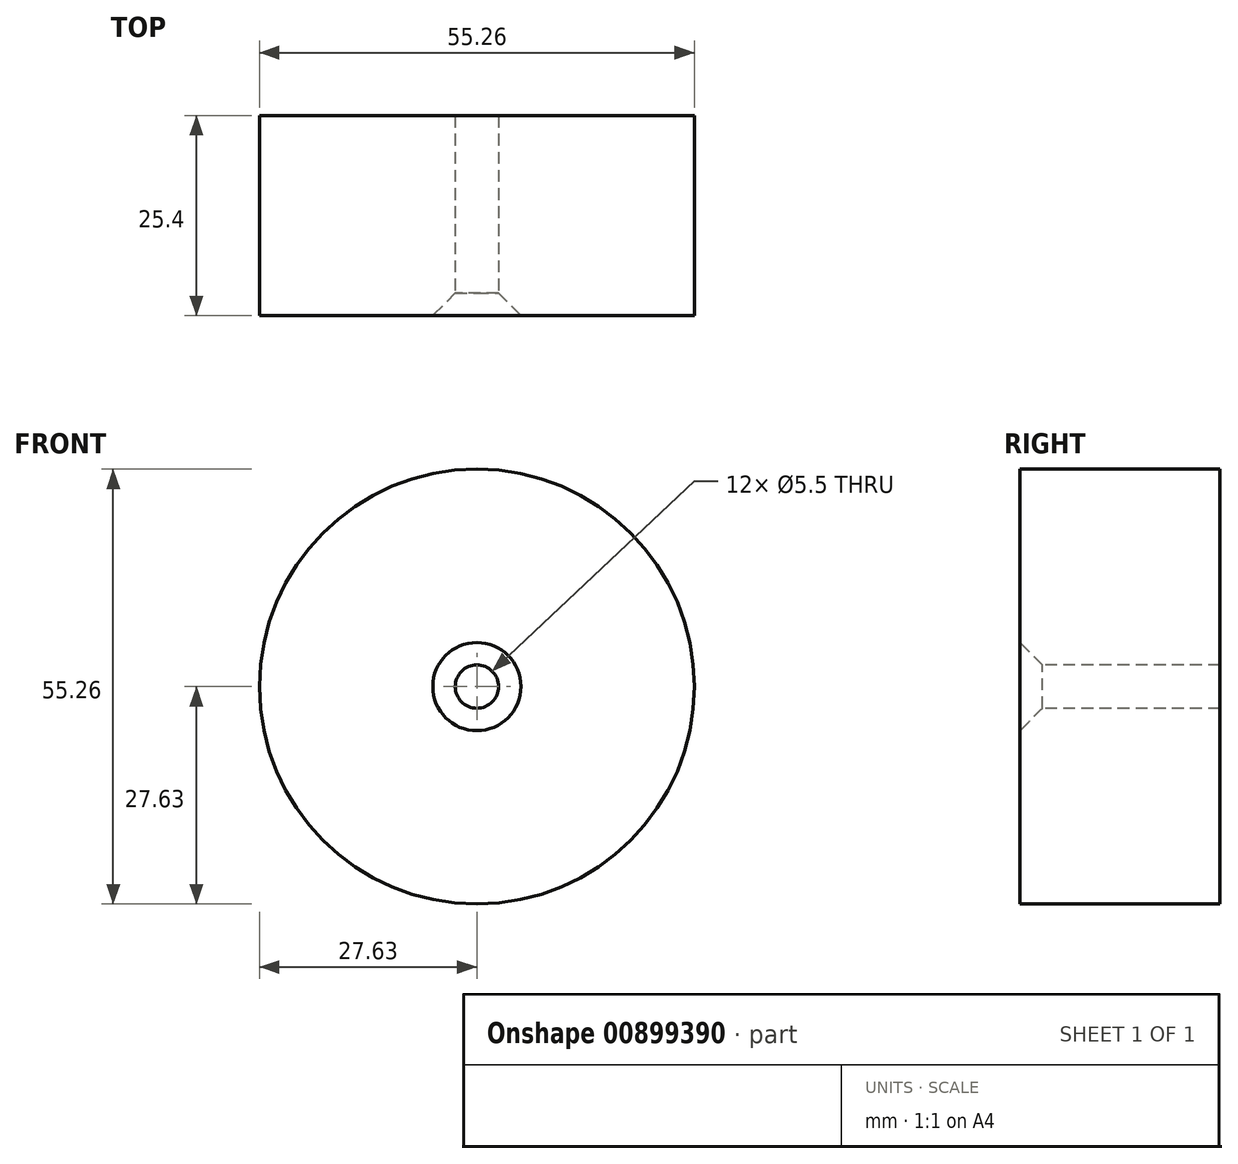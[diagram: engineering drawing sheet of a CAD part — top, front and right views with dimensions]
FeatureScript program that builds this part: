
annotation { "Feature Type Name" : "Feature", "Feature Type Description" : "" }
export const myFeature = defineFeature(function(context is Context, id is Id, definition is map)
    precondition{}
    {
        {
            var Q0;
            Q0=qCreatedBy(makeId("Front.planeOp"),FACE);
            var sketch = newSketch(context, id + "F0", { "sketchPlane" : qUnion([Q0])});
            skCircle(sketch, "E0", {"center": v(0, 0) * mm, "radius": 27.63 * mm});
            skSolve(sketch);
        }
        {
            var Q0;
            Q0=makeQuery(id+"F0.imprint","IMPRINT",FACE,{"disambiguationData":[TD([[makeQuery(id+"F0.imprint","IMPRINT",EDGE,{"derivedFrom":sQuery(id+"F0.wireOp",EDGE,"E0")}),1.0]])]});
            extrude(context, id + "F1", {"entities" : qUnion([Q0]), "depth" : 25.4 * mm, "offsetDistance" : 25.4 * mm});
        }
        {
            var Q0;
            Q0=makeQuery(id+"F1.opExtrude","CAP_FACE",FACE,{"disambiguationData":[OSD([sQuery(id+"F0.wireOp",EDGE,"E0")])],"isStart":false});
            var sketch = newSketch(context, id + "F2", { "sketchPlane" : qUnion([Q0])});
            skPoint(sketch, "E1", {"position": v(0, 0) * mm});
            skSolve(sketch);
        }
        {
            var Q0;
            Q0=sQuery(id+"F2.wireOp",VERTEX,"E1");
            var Q1;
            Q1=makeQuery(id+"F1.opExtrude","SWEPT_BODY",BODY,{"disambiguationData":[OSD([sQuery(id+"F0.wireOp",EDGE,"E0")])]});
            hole(context, id + "F3", {"style" : HoleStyle.C_SINK, "endStyle" : HoleEndStyle.THROUGH, "standardTappedOrClearance" : lookupTablePath({ "fit" : "Normal", "standard" : "ISO", "size" : "M5", "type" : "Clearance" }), "standardBlindInLast" : lookupTablePath({ "fit" : "Normal", "standard" : "ISO", "size" : "M5", "type" : "Clearance" }), "holeDiameter" : 5.5 * mm, "cSinkDiameter" : 11.2 * mm, "cSinkAngle" : 90 * degree, "majorDiameter" : 6.35 * mm, "isTappedThrough" : true, "tappedDepth" : 12.7 * mm, "tapClearance" : 3, "locations" : qUnion([Q0]), "scope" : qUnion([Q1])});
        }
    });
